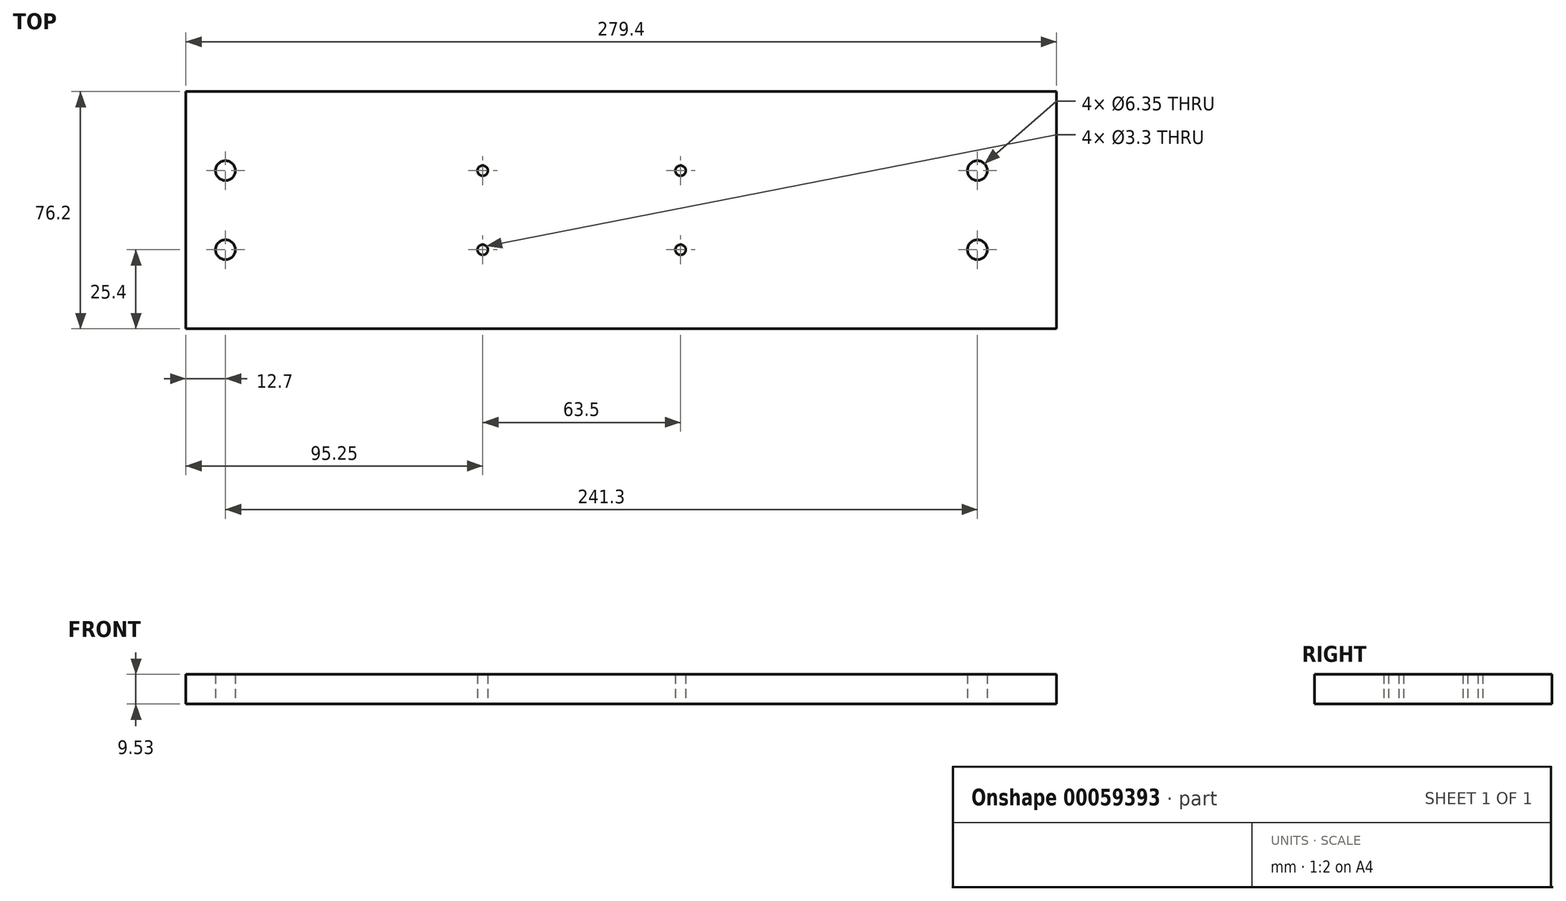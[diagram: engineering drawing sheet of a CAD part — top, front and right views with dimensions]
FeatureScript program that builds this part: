
annotation { "Feature Type Name" : "Feature", "Feature Type Description" : "" }
export const myFeature = defineFeature(function(context is Context, id is Id, definition is map)
    precondition{}
    {
        {
            var Q0;
            Q0=qCreatedBy(makeId("Top.planeOp"),FACE);
            var sketch = newSketch(context, id + "F0", { "sketchPlane" : qUnion([Q0])});
            skLineSegment(sketch, "E0.bottom", {"start": v(0, 0) * mm, "end": v(279.4, 0) * mm});
            skLineSegment(sketch, "E0.top", {"start": v(0, -76.2) * mm, "end": v(279.4, -76.2) * mm});
            skLineSegment(sketch, "E0.left", {"start": v(0, 0) * mm, "end": v(0, -76.2) * mm});
            skLineSegment(sketch, "E0.right", {"start": v(279.4, 0) * mm, "end": v(279.4, -76.2) * mm});
            skLineSegment(sketch, "E1", {"start": v(-13.23, -38.1) * mm, "end": v(297.53, -38.1) * mm, "construction": true});
            skPoint(sketch, "E1.startSnap0", {"position": v(0, -38.1) * mm});
            skCircle(sketch, "E2", {"center": v(12.7, -25.4) * mm, "radius": 3.18 * mm});
            skCircle(sketch, "E3", {"center": v(12.7, -50.8) * mm, "radius": 3.18 * mm});
            skCircle(sketch, "E4", {"center": v(95.25, -25.4) * mm, "radius": 1.65 * mm});
            skCircle(sketch, "E5", {"center": v(95.25, -50.8) * mm, "radius": 1.65 * mm});
            skCircle(sketch, "E6", {"center": v(158.75, -25.4) * mm, "radius": 1.65 * mm});
            skCircle(sketch, "E7", {"center": v(158.75, -50.8) * mm, "radius": 1.65 * mm});
            skCircle(sketch, "E8", {"center": v(254, -50.8) * mm, "radius": 3.18 * mm});
            skCircle(sketch, "E9", {"center": v(254, -25.4) * mm, "radius": 3.18 * mm});
            skSolve(sketch);
        }
        {
            var Q0;
            Q0 = qSketchRegion(id + "F0", true);
            extrude(context, id + "F1", {"entities" : qUnion([Q0]), "depth" : 9.52 * mm});
        }
    });
